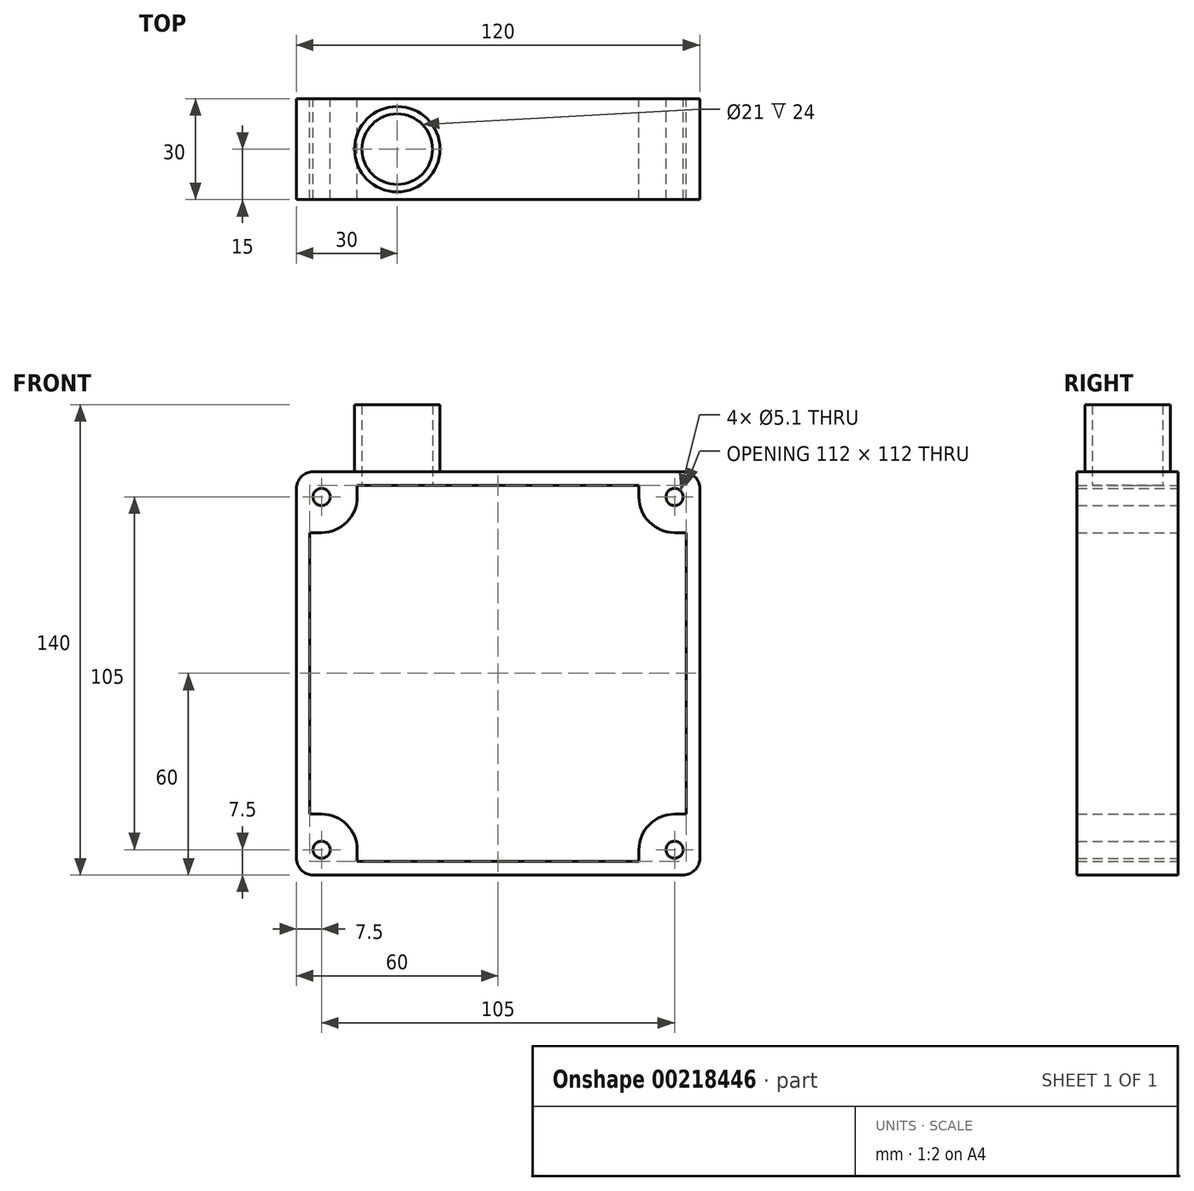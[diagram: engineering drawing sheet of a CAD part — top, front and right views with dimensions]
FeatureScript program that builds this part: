
annotation { "Feature Type Name" : "Feature", "Feature Type Description" : "" }
export const myFeature = defineFeature(function(context is Context, id is Id, definition is map)
    precondition{}
    {
        {
            var Q0;
            Q0=qCreatedBy(makeId("Front.planeOp"),FACE);
            var sketch = newSketch(context, id + "F0", { "sketchPlane" : qUnion([Q0])});
            skLineSegment(sketch, "E0.bottom", {"start": v(5, 0) * mm, "end": v(115, 0) * mm});
            skLineSegment(sketch, "E0.top", {"start": v(5, 120) * mm, "end": v(115, 120) * mm});
            skLineSegment(sketch, "E0.left", {"start": v(0, 5) * mm, "end": v(0, 115) * mm});
            skLineSegment(sketch, "E0.right", {"start": v(120, 5) * mm, "end": v(120, 115) * mm});
            skPoint(sketch, "E0.middle", {"position": v(60, 60) * mm});
            skLineSegment(sketch, "E1.bottom", {"start": v(7.5, 7.5) * mm, "end": v(112.5, 7.5) * mm, "construction": true});
            skLineSegment(sketch, "E1.top", {"start": v(7.5, 112.5) * mm, "end": v(112.5, 112.5) * mm, "construction": true});
            skLineSegment(sketch, "E1.left", {"start": v(7.5, 7.5) * mm, "end": v(7.5, 112.5) * mm, "construction": true});
            skLineSegment(sketch, "E1.right", {"start": v(112.5, 7.5) * mm, "end": v(112.5, 112.5) * mm, "construction": true});
            skArc(sketch, "E2", {"start": v(7.5, 101.9) * mm, "mid": v(15, 105) * mm, "end": v(18.1, 112.5) * mm});
            skArc(sketch, "E3", {"start": v(18.1, 7.5) * mm, "mid": v(15, 15) * mm, "end": v(7.5, 18.1) * mm});
            skArc(sketch, "E4", {"start": v(112.5, 18.1) * mm, "mid": v(105, 15) * mm, "end": v(101.9, 7.5) * mm});
            skArc(sketch, "E5.trimOffspring", {"start": v(101.9, 112.5) * mm, "mid": v(105, 105) * mm, "end": v(112.5, 101.9) * mm});
            skLineSegment(sketch, "E6.bottom", {"start": v(18.1, 116) * mm, "end": v(101.9, 116) * mm});
            skLineSegment(sketch, "E6.top", {"start": v(18.1, 4) * mm, "end": v(101.9, 4) * mm});
            skLineSegment(sketch, "E6.left", {"start": v(4, 101.9) * mm, "end": v(4, 18.1) * mm});
            skLineSegment(sketch, "E6.right", {"start": v(116, 101.9) * mm, "end": v(116, 18.1) * mm});
            skLineSegment(sketch, "E7", {"start": v(7.5, 101.9) * mm, "end": v(4, 101.9) * mm});
            skLineSegment(sketch, "E8", {"start": v(18.1, 112.5) * mm, "end": v(18.1, 116) * mm});
            skLineSegment(sketch, "E9", {"start": v(101.9, 112.5) * mm, "end": v(101.9, 116) * mm});
            skLineSegment(sketch, "E10", {"start": v(112.5, 101.9) * mm, "end": v(116, 101.9) * mm});
            skLineSegment(sketch, "E11", {"start": v(7.5, 18.1) * mm, "end": v(4, 18.1) * mm});
            skLineSegment(sketch, "E12", {"start": v(18.1, 7.5) * mm, "end": v(18.1, 4) * mm});
            skLineSegment(sketch, "E13", {"start": v(101.9, 7.5) * mm, "end": v(101.9, 4) * mm});
            skLineSegment(sketch, "E14", {"start": v(112.5, 18.1) * mm, "end": v(116, 18.1) * mm});
            skPoint(sketch, "E15.orphan", {"position": v(4, 116) * mm});
            skPoint(sketch, "E16.orphan", {"position": v(116, 116) * mm});
            skPoint(sketch, "E17.orphan", {"position": v(4, 4) * mm});
            skPoint(sketch, "E18.orphan", {"position": v(116, 4) * mm});
            skCircle(sketch, "E19", {"center": v(7.5, 112.5) * mm, "radius": 2.55 * mm});
            skCircle(sketch, "E20", {"center": v(112.5, 112.5) * mm, "radius": 2.55 * mm});
            skCircle(sketch, "E21", {"center": v(112.5, 7.5) * mm, "radius": 2.55 * mm});
            skCircle(sketch, "E22", {"center": v(7.5, 7.5) * mm, "radius": 2.55 * mm});
            skPoint(sketch, "E23.visualSharp", {"position": v(120, 120) * mm});
            skArc(sketch, "E23.filletArc", {"start": v(120, 115) * mm, "mid": v(118.54, 118.54) * mm, "end": v(115, 120) * mm});
            skPoint(sketch, "E24.visualSharp", {"position": v(0, 120) * mm});
            skArc(sketch, "E24.filletArc", {"start": v(5, 120) * mm, "mid": v(1.46, 118.54) * mm, "end": v(0, 115) * mm});
            skPoint(sketch, "E25.visualSharp", {"position": v(0, 0) * mm});
            skArc(sketch, "E25.filletArc", {"start": v(0, 5) * mm, "mid": v(1.46, 1.46) * mm, "end": v(5, 0) * mm});
            skPoint(sketch, "E26.visualSharp", {"position": v(120, 0) * mm});
            skArc(sketch, "E26.filletArc", {"start": v(115, 0) * mm, "mid": v(118.54, 1.46) * mm, "end": v(120, 5) * mm});
            skSolve(sketch);
        }
        {
            var Q0;
            Q0=makeQuery(id+"F0.imprint","IMPRINT",FACE,{"disambiguationData":[TD([[makeQuery(id+"F0.imprint","IMPRINT",EDGE,{"derivedFrom":sQuery(id+"F0.wireOp",EDGE,"E0.bottom")}),1.0]])]});
            extrude(context, id + "F1", {"entities" : qUnion([Q0]), "depth" : 30 * mm, "offsetDistance" : 25 * mm});
        }
        {
            var Q0;
            Q0=makeQuery(id+"F1.opExtrude","SWEPT_FACE",FACE,{"disambiguationData":[OSD([sQuery(id+"F0.wireOp",EDGE,"E0.top")])]});
            var sketch = newSketch(context, id + "F2", { "sketchPlane" : qUnion([Q0])});
            skCircle(sketch, "E27", {"center": v(30, -15) * mm, "radius": 12.7 * mm});
            skPoint(sketch, "E27.centerSnap0", {"position": v(5, -15) * mm});
            skCircle(sketch, "E28", {"center": v(30, -15) * mm, "radius": 10.5 * mm});
            skSolve(sketch);
        }
        {
            var Q0;
            Q0=makeQuery(id+"F2.imprint","IMPRINT",FACE,{"disambiguationData":[TD([[makeQuery(id+"F2.imprint","IMPRINT",EDGE,{"derivedFrom":sQuery(id+"F2.wireOp",EDGE,"E27")}),1.0]])]});
            extrude(context, id + "F3", {"entities" : qUnion([Q0]), "operationType" : NewBodyOperationType.ADD, "depth" : 20 * mm, "offsetDistance" : 25 * mm});
        }
        {
            var Q0;
            Q0=makeQuery(id+"F3.boolean.opBoolean","SPLIT",FACE,{"disambiguationData":[TD([makeQuery(id+"F3.opExtrude","SWEPT_FACE",FACE,{"disambiguationData":[OSD([sQuery(id+"F2.wireOp",EDGE,"E28")])]})])],"derivedFrom":makeQuery(id+"F1.opExtrude","SWEPT_FACE",FACE,{"disambiguationData":[OSD([sQuery(id+"F0.wireOp",EDGE,"E0.top")])]})});
            extrude(context, id + "F4", {"entities" : qUnion([Q0]), "operationType" : NewBodyOperationType.REMOVE, "oppositeDirection" : true, "depth" : 25 * mm, "offsetDistance" : 25 * mm});
        }
    });
